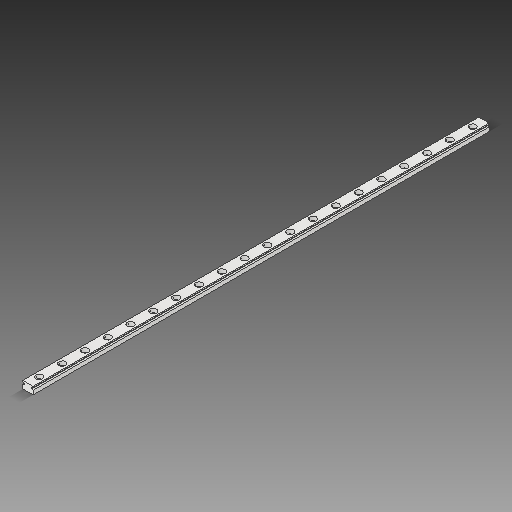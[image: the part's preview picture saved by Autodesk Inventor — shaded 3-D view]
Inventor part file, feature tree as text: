
AUTODESK INVENTOR PART (.ipt)
format: ipt  version: 2017.3 (Build 213256000, 256)  size: 190,464 bytes
history: imported  units: mm
features: other x3, sketch x2, imported_body x1
ambient origin geometry x8: Origin, YZ Plane, XZ Plane, XY Plane, X Axis, Y Axis, Z Axis, Center Point
bodies: Solid1 (imported_parasolid)
feature tree (6):
  other  "MGN9 Rail 400mm.ipt"
  other  "Solid1::MGN9 Rail 400mm.ipt"
  other  "TaggingFeature1"
  sketch  "Sketch1"  dims[d0=10.0mm]
  sketch  "Sketch2"
  imported_body  NMx_Import_Brep_tag  [imported B-rep: ~78 faces, bbox_mm=[9.0, 6.5, 400.0]]
